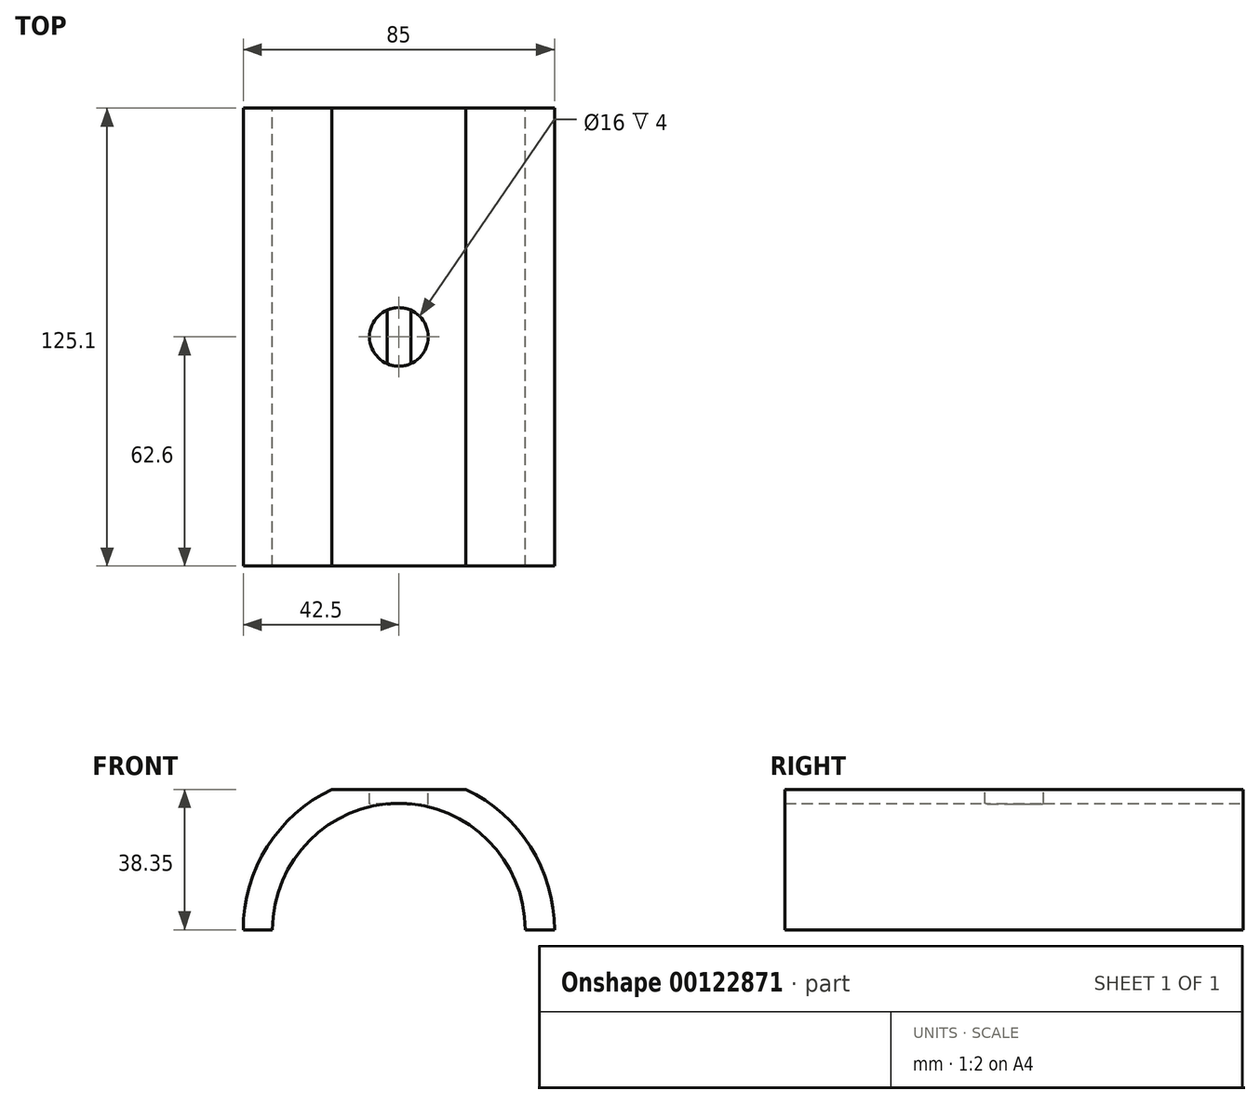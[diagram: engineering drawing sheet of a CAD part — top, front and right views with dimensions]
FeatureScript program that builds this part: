
annotation { "Feature Type Name" : "Feature", "Feature Type Description" : "" }
export const myFeature = defineFeature(function(context is Context, id is Id, definition is map)
    precondition{}
    {
        {
            var Q0;
            Q0=qCreatedBy(makeId("Front.planeOp"),FACE);
            var sketch = newSketch(context, id + "F0", { "sketchPlane" : qUnion([Q0])});
            skCircle(sketch, "E0", {"center": v(0, 0) * mm, "radius": 34.5 * mm});
            skCircle(sketch, "E1", {"center": v(0, 0) * mm, "radius": 42.5 * mm});
            skLineSegment(sketch, "E2", {"start": v(-42.5, 0) * mm, "end": v(42.5, 0) * mm});
            skSolve(sketch);
        }
        {
            var Q0;
            {var subQ0=sQuery(id+"F0.wireOp",EDGE,"E2");var subQ1=sQuery(id+"F0.wireOp",EDGE,"E0");var subQ2=makeQuery(id+"F0.imprint","INTERSECT",VERTEX,{"disambiguationData":[OD(0.0)],"derivedFrom":[subQ1,subQ0]});Q0=makeQuery(id+"F0.imprint","IMPRINT",FACE,{"disambiguationData":[TD([[makeQuery(id+"F0.imprint","IMPRINT",EDGE,{"disambiguationData":[TD([[subQ2,1.0]])],"derivedFrom":subQ1}),-1.0]])]});}
            extrude(context, id + "F1", {"entities" : qUnion([Q0]), "depth" : 125.1 * mm});
        }
        {
            var Q0;
            Q0=qCreatedBy(makeId("Front.planeOp"),FACE);
            var sketch = newSketch(context, id + "F2", { "sketchPlane" : qUnion([Q0])});
            skPoint(sketch, "E3", {"position": v(22, 38.35) * mm});
            skPoint(sketch, "E4", {"position": v(-22, 38.35) * mm});
            skLineSegment(sketch, "E5", {"start": v(-22, 38.35) * mm, "end": v(22, 38.35) * mm});
            skLineSegment(sketch, "E6", {"start": v(22, 45.65) * mm, "end": v(-22, 45.65) * mm});
            skLineSegment(sketch, "E7", {"start": v(-22, 45.65) * mm, "end": v(-22, 38.35) * mm});
            skLineSegment(sketch, "E8", {"start": v(22, 45.65) * mm, "end": v(22, 38.35) * mm});
            skLineSegment(sketch, "E9", {"start": v(0, 45.65) * mm, "end": v(0, 38.35) * mm, "construction": true});
            skLineSegment(sketch, "E10", {"start": v(0, 0) * mm, "end": v(0, 42) * mm, "construction": true});
            skSolve(sketch);
        }
        {
            var Q0;
            Q0=qSketchRegion(id+"F2",true);
            extrude(context, id + "F3", {"entities" : qUnion([Q0]), "operationType" : NewBodyOperationType.REMOVE, "depth" : 125.1 * mm});
        }
        {
            var Q0;
            Q0=makeQuery(id+"F3.boolean.opBoolean","COPY",FACE,{"derivedFrom":makeQuery(id+"F3.opExtrude","SWEPT_FACE",FACE,{"disambiguationData":[OSD([sQuery(id+"F2.wireOp",EDGE,"E5")])]})});
            var sketch = newSketch(context, id + "F4", { "sketchPlane" : qUnion([Q0])});
            skPoint(sketch, "E11", {"position": v(0, -62.5) * mm});
            skCircle(sketch, "E12", {"center": v(0, -62.5) * mm, "radius": 8 * mm});
            skSolve(sketch);
        }
        {
            var Q0;
            Q0=qSketchRegion(id+"F4",true);
            extrude(context, id + "F5", {"entities" : qUnion([Q0]), "operationType" : NewBodyOperationType.REMOVE, "oppositeDirection" : true, "depth" : 4 * mm});
        }
    });
